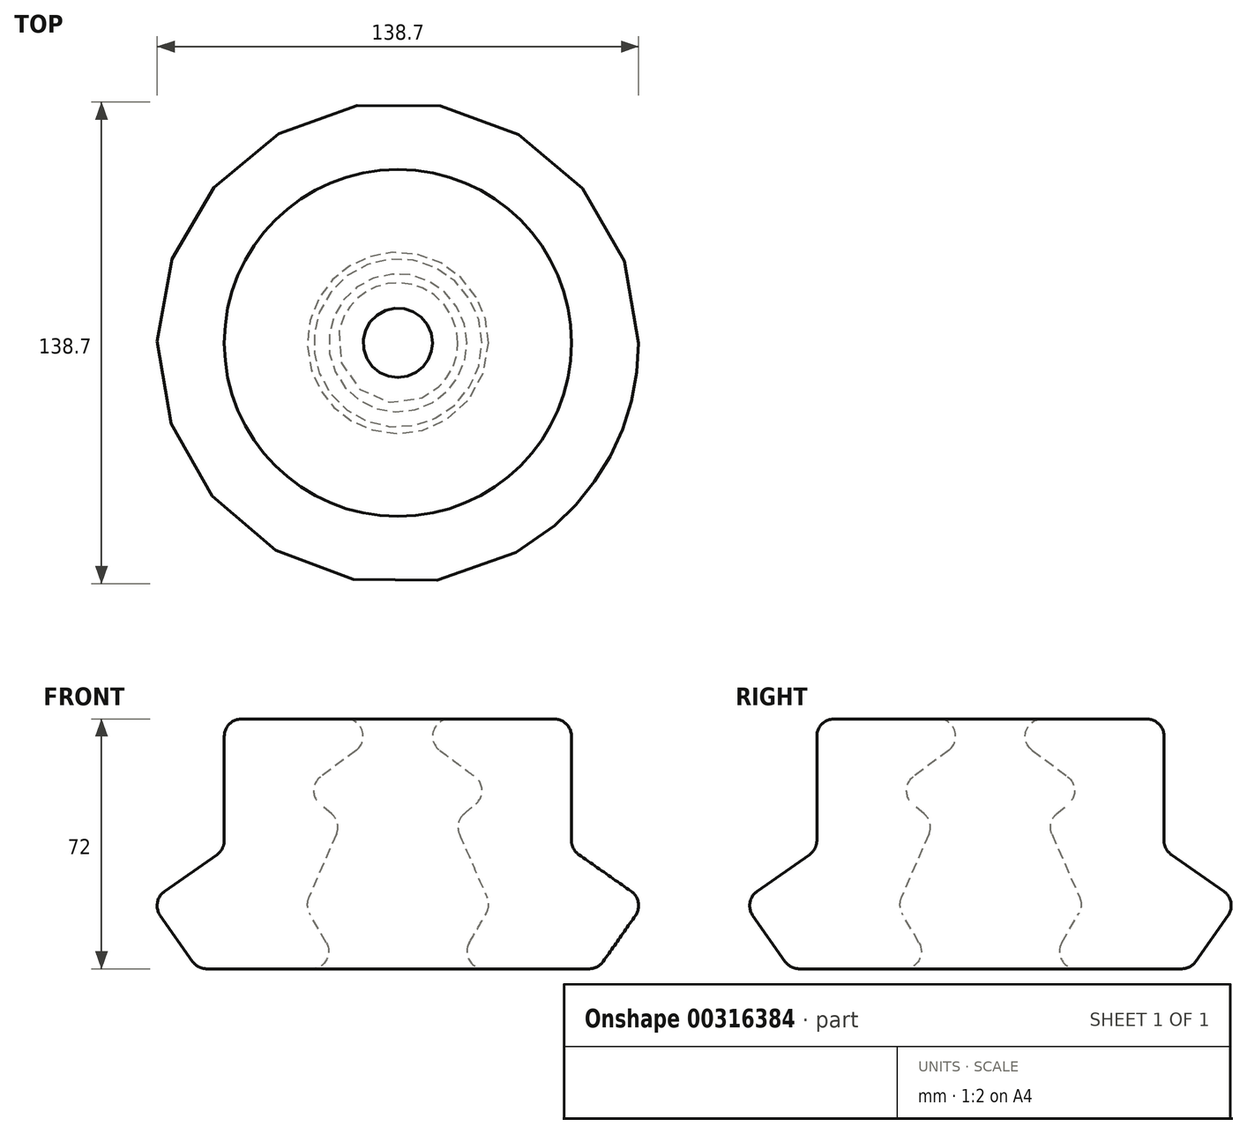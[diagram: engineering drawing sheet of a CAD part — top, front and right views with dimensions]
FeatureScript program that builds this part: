
annotation { "Feature Type Name" : "Feature", "Feature Type Description" : "" }
export const myFeature = defineFeature(function(context is Context, id is Id, definition is map)
    precondition{}
    {
        {
            var Q0;
            Q0=qCreatedBy(makeId("Front.planeOp"),FACE);
            var sketch = newSketch(context, id + "F0", { "sketchPlane" : qUnion([Q0])});
            skLineSegment(sketch, "E0", {"start": v(15, 0) * mm, "end": v(45, 0) * mm});
            skLineSegment(sketch, "E1", {"start": v(50, -5) * mm, "end": v(50, -35) * mm});
            skLineSegment(sketch, "E2", {"start": v(52.13, -39.1) * mm, "end": v(67.22, -49.69) * mm});
            skLineSegment(sketch, "E3", {"start": v(68.45, -56.65) * mm, "end": v(59.17, -69.87) * mm});
            skLineSegment(sketch, "E4", {"start": v(55.08, -72) * mm, "end": v(24.9, -72) * mm});
            skLineSegment(sketch, "E5", {"start": v(20.57, -64.5) * mm, "end": v(25.47, -56.02) * mm});
            skLineSegment(sketch, "E6", {"start": v(25.72, -51.52) * mm, "end": v(17.72, -33.2) * mm});
            skLineSegment(sketch, "E7", {"start": v(19.07, -27.37) * mm, "end": v(22.47, -24.5) * mm});
            skLineSegment(sketch, "E8", {"start": v(22.24, -16.68) * mm, "end": v(12, -9) * mm});
            skPoint(sketch, "E9.visualSharp", {"position": v(27.27, -20.45) * mm});
            skArc(sketch, "E9.filletArc", {"start": v(22.47, -24.5) * mm, "mid": v(24.24, -20.54) * mm, "end": v(22.24, -16.68) * mm});
            skPoint(sketch, "E10.visualSharp", {"position": v(16.23, -29.78) * mm});
            skArc(sketch, "E10.filletArc", {"start": v(19.07, -27.37) * mm, "mid": v(17.43, -30.06) * mm, "end": v(17.72, -33.2) * mm});
            skPoint(sketch, "E11.visualSharp", {"position": v(26.73, -53.84) * mm});
            skArc(sketch, "E11.filletArc", {"start": v(25.47, -56.02) * mm, "mid": v(26.13, -53.8) * mm, "end": v(25.72, -51.52) * mm});
            skPoint(sketch, "E12.visualSharp", {"position": v(16.23, -72) * mm});
            skArc(sketch, "E12.filletArc", {"start": v(20.57, -64.5) * mm, "mid": v(20.56, -69.5) * mm, "end": v(24.9, -72) * mm});
            skPoint(sketch, "E13.visualSharp", {"position": v(57.67, -72) * mm});
            skArc(sketch, "E13.filletArc", {"start": v(55.08, -72) * mm, "mid": v(57.38, -71.44) * mm, "end": v(59.17, -69.87) * mm});
            skPoint(sketch, "E14.visualSharp", {"position": v(71.32, -52.56) * mm});
            skArc(sketch, "E14.filletArc", {"start": v(68.45, -56.65) * mm, "mid": v(69.28, -52.92) * mm, "end": v(67.22, -49.69) * mm});
            skPoint(sketch, "E15.visualSharp", {"position": v(50, -37.6) * mm});
            skArc(sketch, "E15.filletArc", {"start": v(50, -35) * mm, "mid": v(50.56, -37.3) * mm, "end": v(52.13, -39.1) * mm});
            skPoint(sketch, "E16.visualSharp", {"position": v(50, 0) * mm});
            skArc(sketch, "E16.filletArc", {"start": v(50, -5) * mm, "mid": v(48.54, -1.46) * mm, "end": v(45, 0) * mm});
            skPoint(sketch, "E17.visualSharp", {"position": v(0, 0) * mm});
            skArc(sketch, "E17.filletArc", {"start": v(15, 0) * mm, "mid": v(10.26, -3.42) * mm, "end": v(12, -9) * mm});
            skLineSegment(sketch, "E18", {"start": v(0, 74.3) * mm, "end": v(0, -76.2) * mm, "construction": true});
            skSolve(sketch);
        }
        {
            var Q0;
            Q0=makeQuery(id+"F0.imprint","IMPRINT",FACE,{"disambiguationData":[TD([[makeQuery(id+"F0.imprint","IMPRINT",EDGE,{"derivedFrom":sQuery(id+"F0.wireOp",EDGE,"E0")}),-1.0]])]});
            var Q1;
            Q1=sQuery(id+"F0.wireOp",EDGE,"E18");
            revolve(context, id + "F1", {"entities" : qUnion([Q0]), "axis" : qUnion([Q1]), "revolveType" : RevolveType.FULL});
        }
    });
